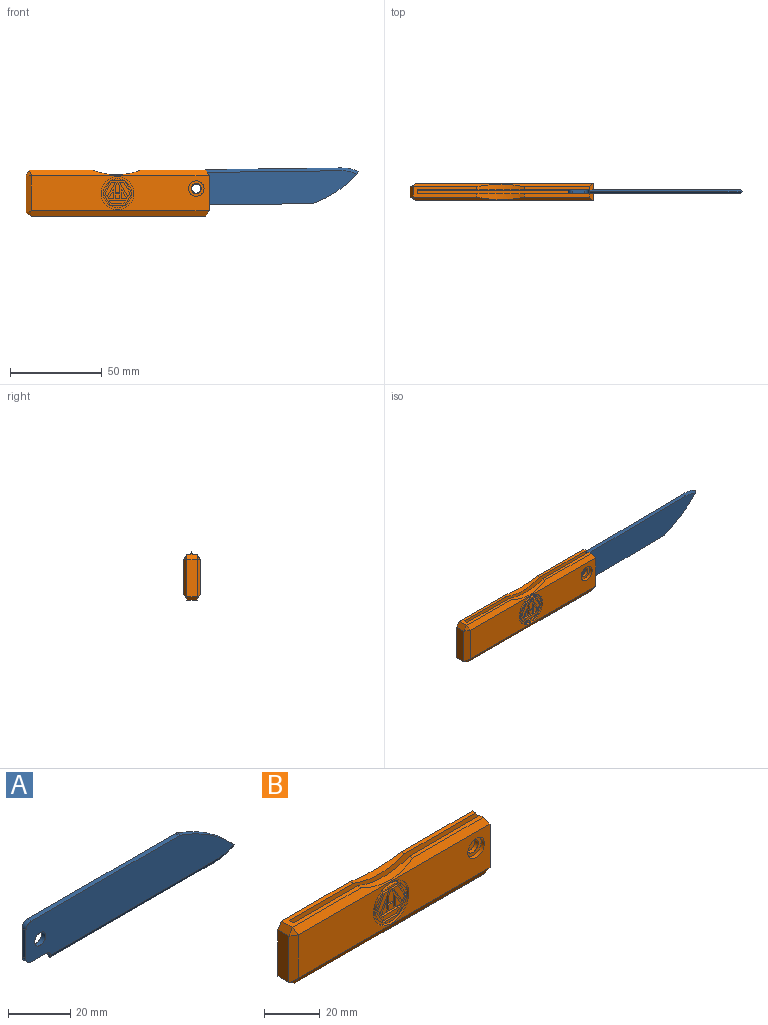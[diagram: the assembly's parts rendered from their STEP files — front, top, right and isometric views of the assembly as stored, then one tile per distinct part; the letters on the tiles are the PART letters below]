
ASSEMBLY  parts=2 mates=1
PART A: 17 faces, bbox 95.1x1.8x19.3 mm
  f0: plane 67.08x1.75mm, normal (0,0,1), area 117.4mm2, adj f6,f7,f11,f12
  f1: plane 11x1.75mm, normal (-1,0,0), area 19.2mm2, adj f6,f7,f8,f12
  f2: plane 6.5x1.75mm, normal (0,0,-1), area 11.4mm2, adj f6,f7,f8,f9
  f3: plane 0.9x0.78mm, normal (-1,0,0), area 0.4mm2, adj f9,f13,f14
  f4: cylinder r=2.5mm len=5mm, axis (0,1,0), area 27.5mm2, adj f6,f7
  f5: cylinder r=60mm len=23.92mm, axis (0,1,0), area 50.5mm2, adj f6,f7,f10,f11
  f6: plane 94.39x17.77mm, normal (0,-1,0), area 1472.3mm2, adj f0,f1,f2,f4,f5,f8,f9,f10
  f7: plane 94.39x17.77mm, normal (0,1,0), area 1472.3mm2, adj f0,f1,f2,f4,f5,f8,f9,f10
  f8: cylinder r=2.5mm len=2.5mm, axis (0,1,0), area 6.9mm2, adj f1,f2,f6,f7
  f9: cylinder r=2.5mm len=2.5mm, axis (0,1,0), area 6.6mm2, adj f2,f3,f6,f7,f13,f14
  f10: cylinder r=2.5mm len=1.75mm, axis (0,1,0), area 1.5mm2, adj f5,f6,f7,f15,f16
  f11: cylinder r=2.5mm len=1.75mm, axis (0,1,0), area 1.5mm2, adj f0,f5,f6,f7
  f12: cylinder r=2.5mm len=2.5mm, axis (0,1,0), area 6.9mm2, adj f0,f1,f6,f7
  f13: plane 74.84x1.52mm, normal (0,-0.87,-0.5), area 130.8mm2, adj f3,f6,f9,f14,f15
  f14: plane 74.84x1.52mm, normal (0,0.87,-0.5), area 130.8mm2, adj f3,f7,f9,f13,f16
  f15: cone r=18.27mm half-angle=60deg, axis (0,1,0), area 15.5mm2, adj f6,f10,f13,f16
  f16: cone r=18.27mm half-angle=60deg, axis (0,-1,0), area 15.5mm2, adj f7,f10,f14,f15
PART B: 102 faces, bbox 100x9x25 mm
  f0: plane 34.81x5.54mm, normal (0,0,1), area 121.1mm2, adj f10,f11,f12,f25,f29,f31,f100,f101
  f1: plane 35.77x1.67mm, normal (0,0,1), area 59.7mm2, adj f10,f21,f25,f101
  f2: plane 97x19mm, normal (0,-1,0), area 1531.8mm2, adj f6,f16,f22,f28,f31,f83
  f3: cylinder r=2.75mm len=5.5mm, axis (0,1,0), area 29.4mm2, adj f12,f17
  f4: cylinder r=2.75mm len=5.5mm, axis (0,1,0), area 29.4mm2, adj f10,f15
  f5: plane 35.77x1.67mm, normal (0,0,1), area 59.7mm2, adj f12,f31,f32,f100
  f6: plane 19x9mm, normal (1,0,0), area 133.6mm2, adj f2,f9,f10,f12,f13,f19,f21,f32
  f7: plane 20.27x5.54mm, normal (-1,0,0), area 112.2mm2, adj f23,f24,f28,f29
  f8: plane 95.27x5.54mm, normal (0,0,-1), area 527.4mm2, adj f18,f19,f22,f23
  f9: plane 97x19mm, normal (0,1,0), area 1786.3mm2, adj f6,f14,f18,f24,f25
  f10: plane 96x20mm, normal (0,-1,0), area 1850.1mm2, adj f0,f1,f4,f6,f11,f13,f21,f101
  f11: plane 20x2.2mm, normal (1,0,0), area 44mm2, adj f0,f10,f12,f13
  f12: plane 96x20mm, normal (0,1,0), area 1850.1mm2, adj f0,f3,f5,f6,f11,f13,f32,f100
  f13: plane 96x2.2mm, normal (0,0,1), area 211.2mm2, adj f6,f10,f11,f12
  f14: cylinder r=4.25mm len=8.5mm, axis (0,1,0), area 45.4mm2, adj f9,f15
  f15: plane 8.5x8.5mm, normal (0,1,0), area 33mm2, adj f4,f14
  f16: cylinder r=4.25mm len=8.5mm, axis (0,-1,0), area 45.4mm2, adj f2,f17
  f17: plane 8.5x8.5mm, normal (0,-1,0), area 33mm2, adj f3,f16
  f18: plane 97x3mm, normal (0,0.87,-0.5), area 333mm2, adj f8,f9,f19,f20
  f19: plane 9x3mm, normal (0.87,0,-0.5), area 25.2mm2, adj f6,f8,f18,f22
  f20: plane 3x3mm, normal (-0.28,0.83,-0.48), area 5.4mm2, adj f18,f23,f24
  f21: plane 3.4x3mm, normal (0.87,0,0.5), area 8.8mm2, adj f1,f6,f10,f25
  f22: plane 97x3mm, normal (0,-0.87,-0.5), area 333mm2, adj f2,f8,f19,f26
  f23: plane 5.54x3mm, normal (-0.5,0,-0.87), area 19.2mm2, adj f7,f8,f20,f26
  f24: plane 20.27x3mm, normal (-0.5,0.87,0), area 68mm2, adj f7,f9,f20,f27
  f25: plane 98.27x3mm, normal (0,0.87,0.5), area 285mm2, adj f0,f1,f9,f21,f27,f101
  f26: plane 3x3mm, normal (-0.28,-0.83,-0.48), area 5.4mm2, adj f22,f23,f28
  f27: plane 3x3mm, normal (-0.48,0.83,0.28), area 5.4mm2, adj f24,f25,f29
  f28: plane 20.27x3mm, normal (-0.5,-0.87,0), area 68mm2, adj f2,f7,f26,f30
  f29: plane 5.54x3mm, normal (-0.87,0,0.5), area 19.2mm2, adj f0,f7,f27,f30
  f30: plane 3x3mm, normal (-0.48,-0.83,0.28), area 5.4mm2, adj f28,f29,f31
  f31: plane 98.27x3mm, normal (0,-0.87,0.5), area 285mm2, adj f0,f2,f5,f30,f32,f100
  f32: plane 3.4x3mm, normal (0.87,0,0.5), area 8.8mm2, adj f5,f6,f12,f31
  f33: plane 2.73x1mm, normal (0,0,-1), area 2.7mm2, adj f34,f85,f86,f99
  f34: plane 4.73x2.73mm, normal (-0.87,0,0.5), area 5.5mm2, adj f33,f85,f86,f99
  f35: plane 2.53x1mm, normal (0,0,1), area 2.5mm2, adj f36,f72,f86,f98
  f36: plane 2.56x1mm, normal (1,0,0), area 2.6mm2, adj f35,f37,f86,f98
  f37: plane 2.53x1mm, normal (0,0,-1), area 2.5mm2, adj f36,f72,f86,f98
  f38: plane 1.01x1mm, normal (0.87,0,-0.5), area 1.2mm2, adj f39,f73,f86,f97
  f39: plane 1.57x1mm, normal (0.5,0,-0.87), area 1.8mm2, adj f38,f40,f86,f97
  f40: plane 5.71x1mm, normal (0,0,-1), area 5.7mm2, adj f39,f41,f86,f97
  f41: plane 1.91x1.11mm, normal (-0.87,0,-0.5), area 2.2mm2, adj f40,f73,f86,f97
  f42: plane 4.73x2.73mm, normal (0.87,0,0.5), area 5.5mm2, adj f43,f74,f86,f96
  f43: plane 2.73x1mm, normal (0,0,-1), area 2.7mm2, adj f42,f74,f86,f96
  f44: plane 7.76x4.48mm, normal (-0.87,0,-0.5), area 9mm2, adj f45,f75,f86,f95
  f45: plane 2.21x1mm, normal (0,0,1), area 2.2mm2, adj f44,f46,f86,f95
  f46: plane 5.85x3.38mm, normal (0.87,0,0.5), area 6.7mm2, adj f45,f75,f86,f95
  f47: plane 2.19x1.27mm, normal (-0.87,0,0.5), area 2.5mm2, adj f48,f76,f86,f94
  f48: plane 2.19x1.27mm, normal (0.87,0,0.5), area 2.5mm2, adj f47,f49,f86,f94
  f49: plane 3.29x1mm, normal (1,0,0), area 3.3mm2, adj f48,f50,f86,f94
  f50: plane 2.53x1mm, normal (0,0,-1), area 2.5mm2, adj f49,f76,f86,f94
  f51: plane 1.91x1.11mm, normal (-0.87,0,-0.5), area 2.2mm2, adj f52,f77,f86,f93
  f52: plane 5.85x3.38mm, normal (-0.87,0,0.5), area 6.7mm2, adj f51,f53,f86,f93
  f53: plane 2.21x1mm, normal (0,0,1), area 2.2mm2, adj f52,f77,f86,f93
  f54: plane 1x0.29mm, normal (-0.5,0,-0.87), area 0.3mm2, adj f55,f78,f86,f92
  f55: cylinder r=7.79mm len=7.18mm, axis (0,-1,0), area 7.5mm2, adj f54,f56,f86,f92
  f56: plane 1x0.29mm, normal (0.5,0,-0.87), area 0.3mm2, adj f55,f78,f86,f92
  f57: cylinder r=7.79mm len=6.21mm, axis (0,-1,0), area 7.5mm2, adj f58,f79,f86,f91
  f58: plane 1x0.29mm, normal (-0.5,0,-0.87), area 0.3mm2, adj f57,f59,f86,f91
  f59: plane 5.71x3.29mm, normal (-0.87,0,-0.5), area 6.6mm2, adj f58,f79,f86,f91
  f60: cylinder r=7.79mm len=6.21mm, axis (0,-1,0), area 7.5mm2, adj f61,f80,f86,f90
  f61: plane 1x0.34mm, normal (-1,0,0), area 0.3mm2, adj f60,f62,f86,f90
  f62: plane 5.71x3.29mm, normal (-0.87,0,0.5), area 6.6mm2, adj f61,f80,f86,f90
  f63: cylinder r=7.79mm len=7.18mm, axis (0,-1,0), area 7.5mm2, adj f64,f81,f86,f89
  f64: plane 1x0.29mm, normal (-0.5,0,0.87), area 0.3mm2, adj f63,f65,f86,f89
  f65: plane 6.59x1mm, normal (0,0,1), area 6.6mm2, adj f64,f81,f86,f89
  f66: plane 1x0.34mm, normal (1,0,0), area 0.3mm2, adj f67,f82,f86,f88
  f67: cylinder r=7.79mm len=6.21mm, axis (0,-1,0), area 7.5mm2, adj f66,f68,f86,f88
  f68: plane 1x0.29mm, normal (0.5,0,0.87), area 0.3mm2, adj f67,f82,f86,f88
  f69: cylinder r=7.79mm len=6.21mm, axis (0,-1,0), area 7.5mm2, adj f70,f84,f86,f87
  f70: plane 1x0.34mm, normal (1,0,0), area 0.3mm2, adj f69,f71,f86,f87
  f71: plane 5.71x3.29mm, normal (0.87,0,-0.5), area 6.6mm2, adj f70,f84,f86,f87
  f72: plane 2.56x1mm, normal (-1,0,0), area 2.6mm2, adj f35,f37,f86,f98
  f73: plane 8.96x1mm, normal (0,0,1), area 9mm2, adj f38,f41,f86,f97
  f74: plane 4.73x1mm, normal (-1,0,0), area 4.7mm2, adj f42,f43,f86,f96
  f75: plane 1.91x1.11mm, normal (0.87,0,-0.5), area 2.2mm2, adj f44,f46,f86,f95
  f76: plane 3.29x1mm, normal (-1,0,0), area 3.3mm2, adj f47,f50,f86,f94
  f77: plane 7.76x4.48mm, normal (0.87,0,-0.5), area 9mm2, adj f51,f53,f86,f93
  f78: plane 6.59x1mm, normal (0,0,-1), area 6.6mm2, adj f54,f56,f86,f92
  f79: plane 1x0.34mm, normal (-1,0,0), area 0.3mm2, adj f57,f59,f86,f91
  f80: plane 1x0.29mm, normal (-0.5,0,0.87), area 0.3mm2, adj f60,f62,f86,f90
  f81: plane 1x0.29mm, normal (0.5,0,0.87), area 0.3mm2, adj f63,f65,f86,f89
  f82: plane 5.71x3.29mm, normal (0.87,0,0.5), area 6.6mm2, adj f66,f68,f86,f88
  f83: cylinder r=9mm len=18mm, axis (0,-1,0), area 56.5mm2, adj f2,f86
  f84: plane 1x0.29mm, normal (0.5,0,-0.87), area 0.3mm2, adj f69,f71,f86,f87
  f85: plane 4.73x1mm, normal (1,0,0), area 4.7mm2, adj f33,f34,f86,f99
  f86: plane 18x18mm, normal (0,-1,0), area 147mm2, adj f33,f34,f35,f36,f37,f38,f39,f40
  f87: plane 6.21x3.59mm, normal (0,-1,0), area 5.4mm2, adj f69,f70,f71,f84
  f88: plane 6.21x3.59mm, normal (0,-1,0), area 5.4mm2, adj f66,f67,f68,f82
  f89: plane 7.18x1.04mm, normal (0,-1,0), area 5.4mm2, adj f63,f64,f65,f81
  f90: plane 6.21x3.59mm, normal (0,-1,0), area 5.4mm2, adj f60,f61,f62,f80
  f91: plane 6.21x3.59mm, normal (0,-1,0), area 5.4mm2, adj f57,f58,f59,f79
  f92: plane 7.18x1.04mm, normal (0,-1,0), area 5.4mm2, adj f54,f55,f56,f78
  f93: plane 7.76x5.58mm, normal (0,-1,0), area 15mm2, adj f51,f52,f53,f77
  f94: plane 5.48x2.53mm, normal (0,-1,0), area 11.1mm2, adj f47,f48,f49,f50,f76
  f95: plane 7.76x5.58mm, normal (0,-1,0), area 15mm2, adj f44,f45,f46,f75
  f96: plane 4.73x2.73mm, normal (0,-1,0), area 6.5mm2, adj f42,f43,f74
  f97: plane 8.96x1.91mm, normal (0,-1,0), area 14.6mm2, adj f38,f39,f40,f41,f73
  f98: plane 2.56x2.53mm, normal (0,-1,0), area 6.5mm2, adj f35,f36,f37,f72
  f99: plane 4.73x2.73mm, normal (0,-1,0), area 6.5mm2, adj f33,f34,f85
  f100: cylinder r=35mm len=25.96mm, axis (0,1,0), area 69.8mm2, adj f0,f5,f12,f31
  f101: cylinder r=35mm len=25.96mm, axis (0,1,0), area 69.8mm2, adj f0,f1,f10,f25
PLACE A rot(axis=(1,0,0.01),180deg) t=(51.8,22.83,8.27)mm
PLACE B t=(-32.19,23.48,4.51)mm fixed
MATE revolute A.f4 <-> B.f3  axis (0,1,0) through (10.81,24.58,7.01)mm
